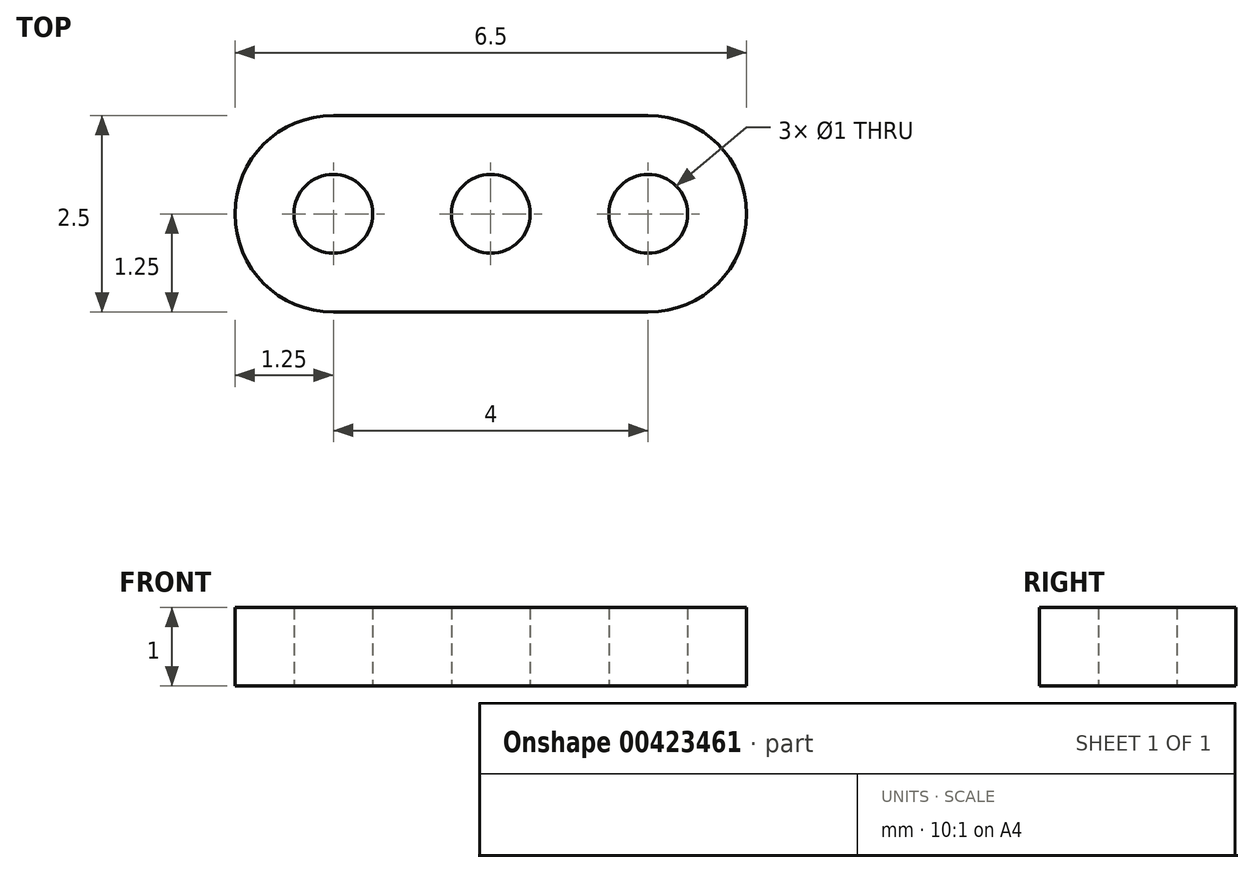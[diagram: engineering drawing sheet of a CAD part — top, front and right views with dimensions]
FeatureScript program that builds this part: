
annotation { "Feature Type Name" : "Feature", "Feature Type Description" : "" }
export const myFeature = defineFeature(function(context is Context, id is Id, definition is map)
    precondition{}
    {
        {
            var Q0;
            Q0=qCreatedBy(makeId("Top.planeOp"),FACE);
            var sketch = newSketch(context, id + "F0", { "sketchPlane" : qUnion([Q0])});
            skCircle(sketch, "E0", {"center": v(0, 0) * mm, "radius": 0.5 * mm});
            skCircle(sketch, "E1", {"center": v(2, 0) * mm, "radius": 0.5 * mm});
            skCircle(sketch, "E2", {"center": v(-2, 0) * mm, "radius": 0.5 * mm});
            skLineSegment(sketch, "E3", {"start": v(-2, -1.25) * mm, "end": v(2, -1.25) * mm});
            skLineSegment(sketch, "E4", {"start": v(-2, 1.25) * mm, "end": v(2, 1.25) * mm});
            skArc(sketch, "E5", {"start": v(-2, -1.25) * mm, "mid": v(-0.75, 0) * mm, "end": v(-2, 1.25) * mm, "construction": true});
            skArc(sketch, "E6", {"start": v(-2, 1.25) * mm, "mid": v(-3.25, 0) * mm, "end": v(-2, -1.25) * mm});
            skArc(sketch, "E7", {"start": v(2, 1.25) * mm, "mid": v(0.75, 0) * mm, "end": v(2, -1.25) * mm, "construction": true});
            skArc(sketch, "E8", {"start": v(2, -1.25) * mm, "mid": v(3.25, 0) * mm, "end": v(2, 1.25) * mm});
            skSolve(sketch);
        }
        {
            var Q0;
            Q0 = qSketchRegion(id + "F0", true);
            extrude(context, id + "F1", {"entities" : qUnion([Q0]), "depth" : 1 * mm, "offsetDistance" : 25 * mm});
        }
    });
